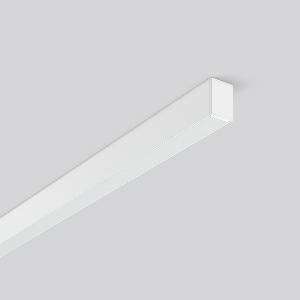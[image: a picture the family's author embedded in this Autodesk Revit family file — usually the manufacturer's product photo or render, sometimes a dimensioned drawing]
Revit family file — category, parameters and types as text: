
# Revit family: less_is_more_27_312196_002_1_dc89
name_source: partatom
category: Lighting Fixtures
units: mm (PartAtom-declared; Revit-internal decimal feet)

## family parameters
Cut with Voids When Loaded = No
Host = Face
Light Source = No
Part Type = Normal
Room Calculation Point = No
Round Connector Dimension = Use Diameter
Shared = No

## types (1)
- LESS IS MORE 27 (1 x LED Modul 840, 1950 lm, 4000)
    Apparent Load = 25 VA
    CIE Flux Codes = 48 79 96 100 100
    Color Rendering = 80
    Color Temperature = 4000
    Default Elevation = 1800 mm
    Description = Series: LESS IS MORE 27
Ceiling and wall luminaire with slim design. Housing: extruded aluminium profile, powder-coated. End cap aluminium powder-coated. Diffuser made of non-yellowing plastic (PMMA), opal. Suitable for Ceiling mounting, Wall (surface). External driver with connecting cable. 
Colour: traffic white, matt (RAL 9016)
Length: 1012 mm
Width: 28 mm
Height: 38 mm
Lamp: LED
Socket: without socket
Colour temperature: 4000K
Colour rendering index (CRI): 82
System power: 25 W
Rated luminous flux: 1950 lm
Luminous efficiency: 78 lm/W
Control gear: Regulated power supply
Protection class: II
Type of protection: IP 20
    Height = 38 mm
    Lamp = 1 x LED Modul 840
    Lamp Light Flux = 1950 lm
    Lamp count = 1
    Length = 1012 mm
    Lifetime = 50000 h
    Luminous efficacy = 78 lm/W
    Manufacturer = RZB
    ModVariant = No
    Model = 312196.002.1
    Mounting Place = Ceiling, Wall
    Mounting Type = Surface mounted
    Number of Poles = 1
    OnlyDefault = Yes
    Power Factor = 1
    Product Name = LESS IS MORE 27
    Product group = Surface mounted LED linear luminaires
    ProductGroupID = 307
    Protection Class = Protection class II
    Protection Degree = IP 20
    RLX_Detail_Level = 1
    RLX_Emergency_Light_Flux = 0 lm
    RLX_Emergency_Type = 0
    RLX_Emergency_Type_DB = No
    RlxData = <blob elided: 22781 chars, md5=1c8c53f1>
    Socket = socket
    Standby Power = 0 W
    System Light Flux = 1950 lm
    System Power = 25 W
    Type Comments = Product without accessories
    Type Image = 312196.002.jpg
    URL = http://relux.com
    VarID = ---
    Voltage = 230 V
    Voltage Range = 220-240 V
    Weight = 0.00 kg
    Width = 28 mm

## geometry (parser evidence)
native form markers: Blend x4, Sweep x12
no freeform markers — native parametric forms only
